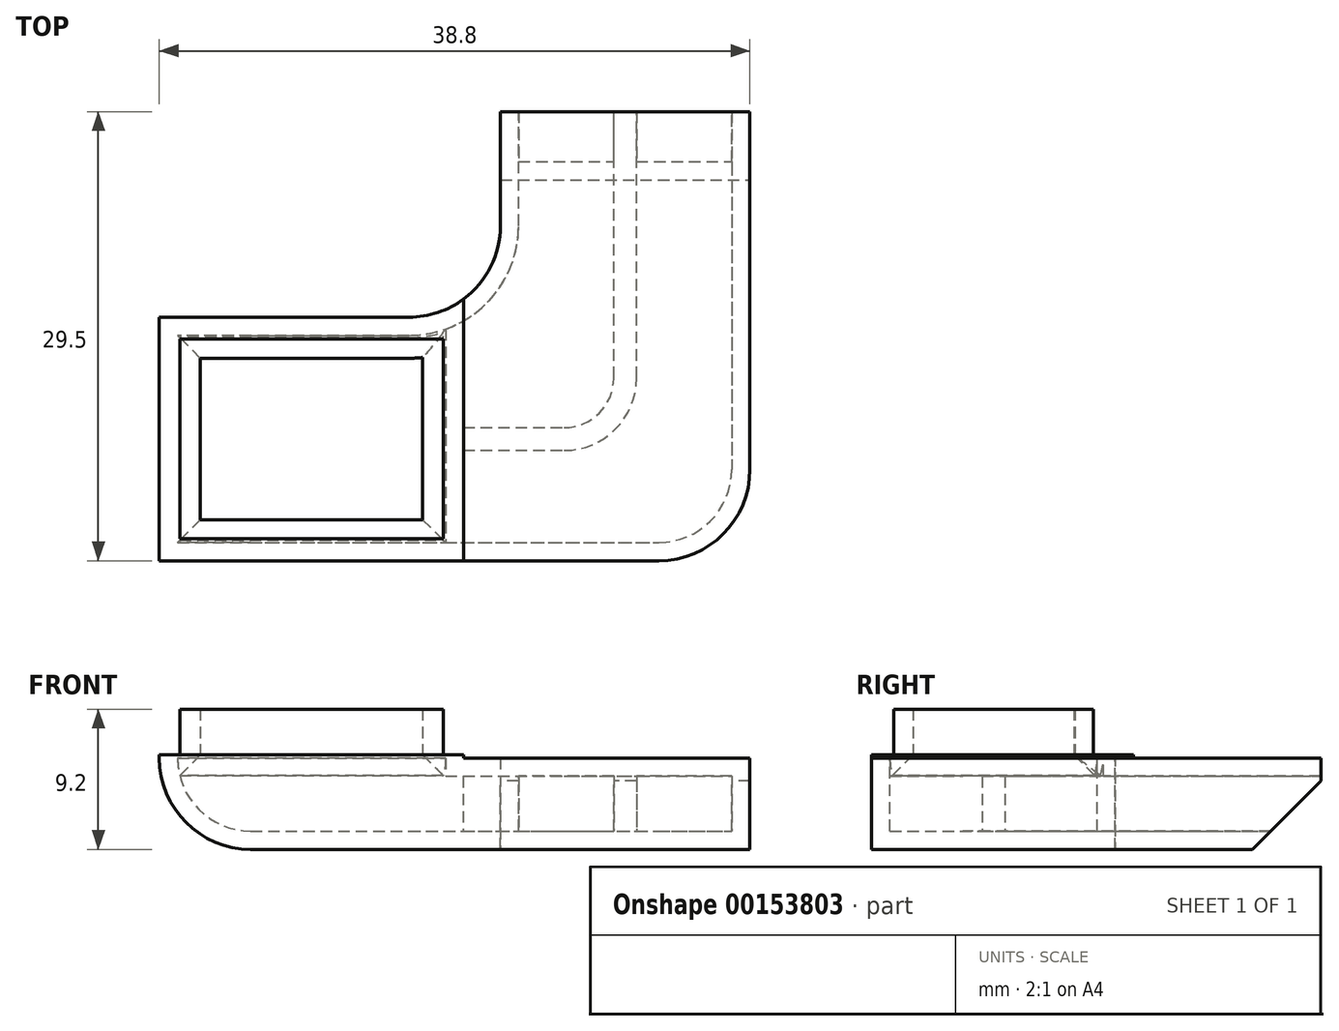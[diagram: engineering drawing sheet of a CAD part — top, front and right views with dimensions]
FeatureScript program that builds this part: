
annotation { "Feature Type Name" : "Feature", "Feature Type Description" : "" }
export const myFeature = defineFeature(function(context is Context, id is Id, definition is map)
    precondition{}
    {
        {
            var Q0;
            Q0=qCreatedBy(makeId("Top.planeOp"),FACE);
            var sketch = newSketch(context, id + "F0", { "sketchPlane" : qUnion([Q0])});
            skLineSegment(sketch, "E0.bottom", {"start": v(-19.4, 8) * mm, "end": v(3, 8) * mm});
            skLineSegment(sketch, "E0.top", {"start": v(-19.4, -8) * mm, "end": v(19.4, -8) * mm});
            skLineSegment(sketch, "E0.left", {"start": v(-19.4, 8) * mm, "end": v(-19.4, -8) * mm});
            skLineSegment(sketch, "E0.right", {"start": v(19.4, 8) * mm, "end": v(19.4, -8) * mm});
            skPoint(sketch, "E0.middle", {"position": v(0, 0) * mm});
            skLineSegment(sketch, "E1.top", {"start": v(19.4, 21.5) * mm, "end": v(3, 21.5) * mm});
            skLineSegment(sketch, "E1.left", {"start": v(19.4, 8) * mm, "end": v(19.4, 21.5) * mm});
            skLineSegment(sketch, "E1.right", {"start": v(3, 8) * mm, "end": v(3, 21.5) * mm});
            skSolve(sketch);
        }
        {
            var Q0;
            Q0 = qSketchRegion(id + "F0", true);
            extrude(context, id + "F1", {"entities" : qUnion([Q0]), "depth" : 6 * mm, "offsetDistance" : 25 * mm});
        }
        {
            var Q0;
            Q0=makeQuery(id+"F1.opExtrude","CAP_FACE",FACE,{"disambiguationData":[OSD([sQuery(id+"F0.wireOp",EDGE,"E0.bottom"),sQuery(id+"F0.wireOp",EDGE,"E0.top"),sQuery(id+"F0.wireOp",EDGE,"E0.left"),sQuery(id+"F0.wireOp",EDGE,"E0.right"),sQuery(id+"F0.wireOp",EDGE,"E1.top"),sQuery(id+"F0.wireOp",EDGE,"E1.left"),sQuery(id+"F0.wireOp",EDGE,"E1.right")])],"isStart":false});
            var sketch = newSketch(context, id + "F2", { "sketchPlane" : qUnion([Q0])});
            skLineSegment(sketch, "E2.bottom", {"start": v(-19.4, 8) * mm, "end": v(0.6, 8) * mm});
            skLineSegment(sketch, "E2.top", {"start": v(-19.4, -8) * mm, "end": v(0.6, -8) * mm});
            skLineSegment(sketch, "E2.left", {"start": v(-19.4, 8) * mm, "end": v(-19.4, -8) * mm});
            skLineSegment(sketch, "E2.right", {"start": v(0.6, 8) * mm, "end": v(0.6, -8) * mm});
            skSolve(sketch);
        }
        {
            var Q0;
            Q0 = qSketchRegion(id + "F2", true);
            extrude(context, id + "F3", {"entities" : qUnion([Q0]), "operationType" : NewBodyOperationType.ADD, "depth" : 0.2 * mm, "offsetDistance" : 25 * mm});
        }
        {
            var Q0;
            Q0=makeQuery(id+"F1.opExtrude","SWEPT_EDGE",EDGE,{"disambiguationData":[OSD([sQuery(id+"F0.wireOp",EDGE,"E0.top"),sQuery(id+"F0.wireOp",EDGE,"E0.right")])]});
            var Q1;
            Q1=makeQuery(id+"F1.opExtrude","SWEPT_EDGE",EDGE,{"disambiguationData":[OSD([sQuery(id+"F0.wireOp",EDGE,"E0.bottom"),sQuery(id+"F0.wireOp",EDGE,"E1.right")])]});
            var Q2;
            Q2=makeQuery(id+"F1.opExtrude","CAP_EDGE",EDGE,{"disambiguationData":[OSD([sQuery(id+"F0.wireOp",EDGE,"E0.left")])],"isStart":true});
            fillet(context, id + "F4", {"entities" : qUnion([Q0, Q1, Q2]), "radius" : 6 * mm, "tangentPropagation" : true, "allowEdgeOverflow" : false});
        }
        {
            var Q0;
            Q0=makeQuery(id+"F1.opExtrude","SWEPT_FACE",FACE,{"disambiguationData":[OSD([sQuery(id+"F0.wireOp",EDGE,"E1.top")])]});
            var Q1;
            Q1=makeQuery(id+"F3.opExtrude","CAP_FACE",FACE,{"disambiguationData":[OSD([sQuery(id+"F2.wireOp",EDGE,"E2.bottom"),sQuery(id+"F2.wireOp",EDGE,"E2.top"),sQuery(id+"F2.wireOp",EDGE,"E2.left"),sQuery(id+"F2.wireOp",EDGE,"E2.right")])],"isStart":false});
            shell(context, id + "F5", {"entities" : qUnion([Q0, Q1]), "thickness" : 1.2 * mm});
        }
        {
            var Q0;
            Q0=qCreatedBy(makeId("Top.planeOp"),FACE);
            var sketch = newSketch(context, id + "F6", { "sketchPlane" : qUnion([Q0])});
            skLineSegment(sketch, "E3", {"start": v(11.2, 21.5) * mm, "end": v(11.2, 4) * mm, "construction": true});
            skLineSegment(sketch, "E4", {"start": v(7.2, 0) * mm, "end": v(0.56, 0) * mm, "construction": true});
            skPoint(sketch, "E5.visualSharp", {"position": v(11.2, 0) * mm});
            skArc(sketch, "E5.filletArc", {"start": v(7.2, 0) * mm, "mid": v(10.03, 1.17) * mm, "end": v(11.2, 4) * mm, "construction": true});
            skLineSegment(sketch, "E6.0", {"start": v(7.2, 0.75) * mm, "end": v(0.56, 0.75) * mm});
            skArc(sketch, "E6.1", {"start": v(7.2, 0.75) * mm, "mid": v(9.5, 1.7) * mm, "end": v(10.45, 4) * mm});
            skLineSegment(sketch, "E6.2", {"start": v(10.45, 21.5) * mm, "end": v(10.45, 4) * mm});
            skLineSegment(sketch, "E7.0", {"start": v(7.2, -0.75) * mm, "end": v(0.56, -0.75) * mm});
            skArc(sketch, "E7.1", {"start": v(7.2, -0.75) * mm, "mid": v(10.56, 0.64) * mm, "end": v(11.95, 4) * mm});
            skLineSegment(sketch, "E7.2", {"start": v(11.95, 21.5) * mm, "end": v(11.95, 4) * mm});
            skLineSegment(sketch, "E8", {"start": v(10.45, 21.5) * mm, "end": v(11.95, 21.5) * mm});
            skLineSegment(sketch, "E9", {"start": v(0.56, 0.75) * mm, "end": v(0.56, -0.75) * mm});
            skSolve(sketch);
        }
        {
            var Q0;
            Q0 = qSketchRegion(id + "F6", true);
            extrude(context, id + "F7", {"entities" : qUnion([Q0]), "operationType" : NewBodyOperationType.ADD, "depth" : 5 * mm, "offsetDistance" : 25 * mm});
        }
        {
            var Q0;
            Q0=makeQuery(id+"F5.opShell","OFFSET_FACE",FACE,{"disambiguationData":[OSD([sQuery(id+"F0.wireOp",EDGE,"E0.bottom"),sQuery(id+"F2.wireOp",EDGE,"E2.bottom")])]});
            var sketch = newSketch(context, id + "F8", { "sketchPlane" : qUnion([Q0])});
            skLineSegment(sketch, "E10", {"start": v(-18.2, 6.2) * mm, "end": v(-16.7, 6.2) * mm});
            skLineSegment(sketch, "E11", {"start": v(-16.7, 6.2) * mm, "end": v(-18.2, 4.7) * mm});
            skLineSegment(sketch, "E12", {"start": v(-18.2, 4.7) * mm, "end": v(-18.2, 6.2) * mm});
            skSolve(sketch);
        }
        {
            var Q0;
            Q0=makeQuery(id+"F8.imprint","IMPRINT",FACE,{"disambiguationData":[TD([[makeQuery(id+"F8.imprint","IMPRINT",EDGE,{"derivedFrom":sQuery(id+"F8.wireOp",EDGE,"E10")}),-1.0]])]});
            var Q1;
            Q1=makeQuery(id+"F5.opShell","OFFSET_EDGE",EDGE,{"disambiguationData":[OSD([sQuery(id+"F2.wireOp",EDGE,"E2.left")])]});
            var Q2;
            Q2=makeQuery(id+"F5.opShell","OFFSET_EDGE",EDGE,{"disambiguationData":[OSD([sQuery(id+"F2.wireOp",EDGE,"E2.top")])]});
            var Q3;
            Q3=makeQuery(id+"F5.opShell","OFFSET_EDGE",EDGE,{"disambiguationData":[OSD([sQuery(id+"F2.wireOp",EDGE,"E2.bottom")])]});
            var Q4;
            {var subQ0=sQuery(id+"F2.wireOp",EDGE,"E2.right");Q4=makeQuery(id+"F5.opShell","OFFSET_EDGE",EDGE,{"disambiguationData":[OSD([subQ0]),TDD([makeQuery(id+"F3.opExtrude","CAP_EDGE",EDGE,{"disambiguationData":[OSD([subQ0])],"isStart":false})])]});}
            var Q5;
            Q5=makeQuery(id+"F5.opShell","OFFSET_EDGE",EDGE,{"disambiguationData":[OSD([sQuery(id+"F0.wireOp",EDGE,"E0.bottom"),sQuery(id+"F0.wireOp",EDGE,"E1.right"),sQuery(id+"F2.wireOp",EDGE,"E2.bottom"),sQuery(id+"F2.wireOp",EDGE,"E2.top"),sQuery(id+"F2.wireOp",EDGE,"E2.left"),sQuery(id+"F2.wireOp",EDGE,"E2.right")])]});
            sweep(context, id + "F9", {"operationType" : NewBodyOperationType.ADD, "profiles" : qUnion([Q0]), "path" : qUnion([Q1, Q2, Q3, Q4, Q5])});
        }
        {
            var Q0;
            {var subQ0=sQuery(id+"F2.wireOp",EDGE,"E2.left");Q0=makeQuery(id+"F9.boolean.opBoolean","MERGE",FACE,{"derivedFrom":[makeQuery(id+"F3.opExtrude","CAP_FACE",FACE,{"disambiguationData":[OSD([sQuery(id+"F2.wireOp",EDGE,"E2.bottom"),sQuery(id+"F2.wireOp",EDGE,"E2.top"),subQ0,sQuery(id+"F2.wireOp",EDGE,"E2.right")])],"isStart":false}),makeQuery(id+"F9.opSweep","SWEPT_FACE",FACE,{"disambiguationData":[OSD([subQ0,sQuery(id+"F8.wireOp",EDGE,"E10")])]})]});}
            var sketch = newSketch(context, id + "F10", { "sketchPlane" : qUnion([Q0])});
            skLineSegment(sketch, "E13.bottom", {"start": v(-2.1, -5.3) * mm, "end": v(-16.7, -5.3) * mm});
            skLineSegment(sketch, "E13.top", {"start": v(-2.1, 5.3) * mm, "end": v(-16.7, 5.3) * mm});
            skLineSegment(sketch, "E13.left", {"start": v(-2.1, -5.3) * mm, "end": v(-2.1, 5.3) * mm});
            skLineSegment(sketch, "E13.right", {"start": v(-16.7, -5.3) * mm, "end": v(-16.7, 5.3) * mm});
            skLineSegment(sketch, "E14.bottom", {"start": v(-0.75, -6.55) * mm, "end": v(-18.05, -6.55) * mm});
            skLineSegment(sketch, "E14.top", {"start": v(-0.75, 6.55) * mm, "end": v(-18.05, 6.55) * mm});
            skLineSegment(sketch, "E14.left", {"start": v(-0.75, -6.55) * mm, "end": v(-0.75, 6.55) * mm});
            skLineSegment(sketch, "E14.right", {"start": v(-18.05, -6.55) * mm, "end": v(-18.05, 6.55) * mm});
            skPoint(sketch, "E15", {"position": v(-9.4, -6.55) * mm});
            skPoint(sketch, "E16", {"position": v(-18.05, 0) * mm});
            skPoint(sketch, "E17", {"position": v(-9.4, -5.3) * mm});
            skPoint(sketch, "E18", {"position": v(-16.7, 0) * mm});
            skSolve(sketch);
        }
        {
            var Q0;
            Q0=makeQuery(id+"F10.imprint","IMPRINT",FACE,{"disambiguationData":[TD([[makeQuery(id+"F10.imprint","IMPRINT",EDGE,{"derivedFrom":sQuery(id+"F10.wireOp",EDGE,"E13.bottom")}),-1.0]])]});
            extrude(context, id + "F11", {"entities" : qUnion([Q0]), "operationType" : NewBodyOperationType.ADD, "depth" : 3 * mm, "offsetDistance" : 25 * mm});
        }
        {
            var Q0;
            Q0=makeQuery(id+"F1.opExtrude","CAP_EDGE",EDGE,{"disambiguationData":[OSD([sQuery(id+"F0.wireOp",EDGE,"E1.top")])],"isStart":true});
            chamfer(context, id + "F12", {"entities" : qUnion([Q0]), "width" : 4.5 * mm, "tangentPropagation" : true});
        }
    });
